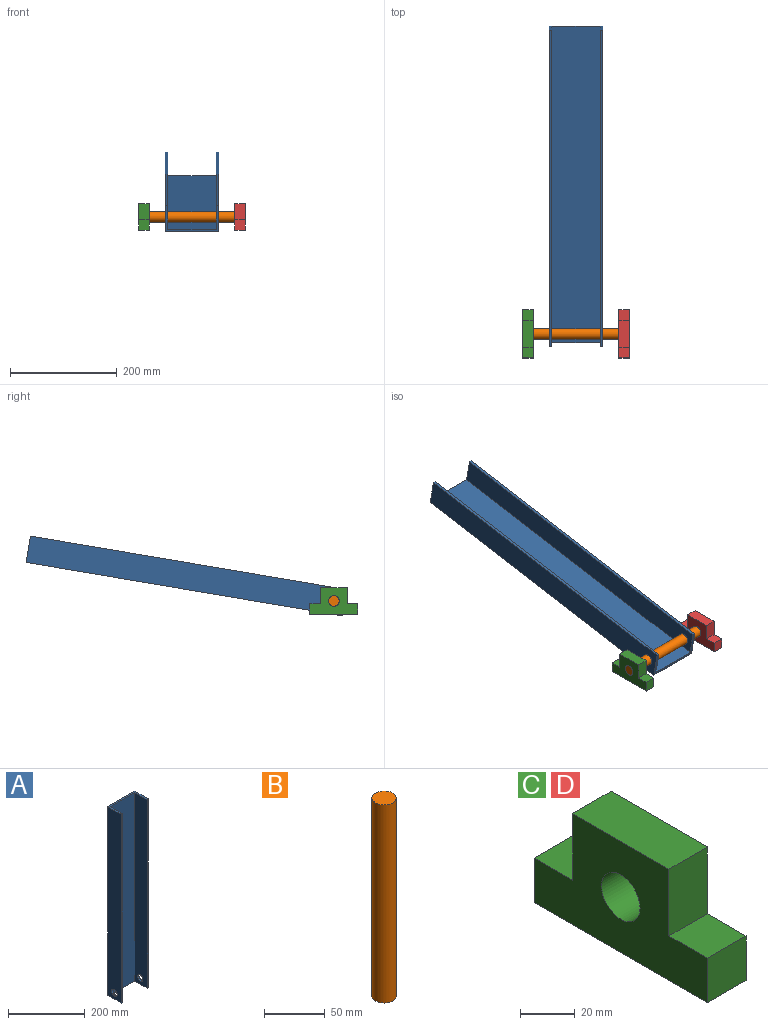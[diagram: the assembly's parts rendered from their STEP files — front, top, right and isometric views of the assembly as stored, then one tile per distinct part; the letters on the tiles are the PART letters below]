
ASSEMBLY  parts=4 mates=3
PART A: 12 faces, bbox 100x50x600 mm
  f0: cylinder r=10mm len=20mm, axis (1,0,0), area 314.2mm2, adj f3,f5
  f1: plane 600x45mm, normal (1,0,0), area 26685.8mm2, adj f2,f8,f9,f10,f11
  f2: plane 600x90mm, normal (0,-1,0), area 54000mm2, adj f1,f3,f9,f10
  f3: plane 600x45mm, normal (-1,0,0), area 26685.8mm2, adj f0,f2,f4,f9,f10
  f4: plane 600x5mm, normal (0,-1,0), area 3000mm2, adj f3,f5,f9,f10
  f5: plane 600x50mm, normal (1,0,0), area 29685.8mm2, adj f0,f4,f6,f9,f10
  f6: plane 600x100mm, normal (0,1,0), area 60000mm2, adj f5,f7,f9,f10
  f7: plane 600x50mm, normal (-1,0,0), area 29685.8mm2, adj f6,f8,f9,f10,f11
  f8: plane 600x5mm, normal (0,-1,0), area 3000mm2, adj f1,f7,f9,f10
  f9: plane 100x50mm, normal (0,0,1), area 950mm2, adj f1,f2,f3,f4,f5,f6,f7,f8
  f10: plane 100x50mm, normal (0,0,-1), area 950mm2, adj f1,f2,f3,f4,f5,f6,f7,f8
  f11: cylinder r=10mm len=20mm, axis (-1,0,0), area 314.2mm2, adj f1,f7
PART B: 3 faces, bbox 20x20x200 mm
  f0: cylinder r=10mm len=200mm, axis (0,0,-1), area 12566.4mm2, adj f1,f2
  f1: plane 20x20mm, normal (0,0,1), area 314.2mm2, adj f0
  f2: plane 20x20mm, normal (0,0,-1), area 314.2mm2, adj f0
PART C: 11 faces, bbox 20x90x50 mm
  f0: plane 20x20mm, normal (0,0,1), area 400mm2, adj f1,f2,f3,f7
  f1: plane 90x50mm, normal (-1,0,0), area 2985.8mm2, adj f0,f2,f4,f5,f6,f7,f8,f9
  f2: plane 20x20mm, normal (0,-1,0), area 400mm2, adj f0,f1,f3,f6
  f3: plane 90x50mm, normal (1,0,0), area 2985.8mm2, adj f0,f2,f4,f5,f6,f7,f8,f9
  f4: plane 20x20mm, normal (0,1,0), area 400mm2, adj f1,f3,f5,f6
  f5: plane 20x20mm, normal (0,0,1), area 400mm2, adj f1,f3,f4,f8
  f6: plane 90x20mm, normal (0,0,-1), area 1800mm2, adj f1,f2,f3,f4
  f7: plane 30x20mm, normal (0,-1,0), area 600mm2, adj f0,f1,f3,f9
  f8: plane 30x20mm, normal (0,1,0), area 600mm2, adj f1,f3,f5,f9
  f9: plane 50x20mm, normal (0,0,1), area 1000mm2, adj f1,f3,f7,f8
  f10: cylinder r=10mm len=20mm, axis (-1,0,0), area 1256.6mm2, adj f1,f3
PART D: same geometry as C
PLACE A rot(axis=(-1,0,0),80.4deg) t=(39.97,-89.68,-49.35)mm
PLACE B rot(axis=(-0.54,-0.64,0.54),114.6deg) t=(139.97,-163.28,-55.2)mm
PLACE C t=(-31.51,-156.87,-46.36)mm fixed
PLACE D t=(148.49,-156.87,-46.36)mm fixed
MATE revolute B.f0 <-> C.f10  axis (-1,0,0) through (-60.03,-74.14,-21.36)mm
MATE fastened B.f0 <-> A.f0  axis (-1,0,0) through (-60.03,-74.14,-21.36)mm
MATE revolute B.f0 <-> D.f10  axis (1,0,0) through (139.97,-74.14,-21.36)mm
